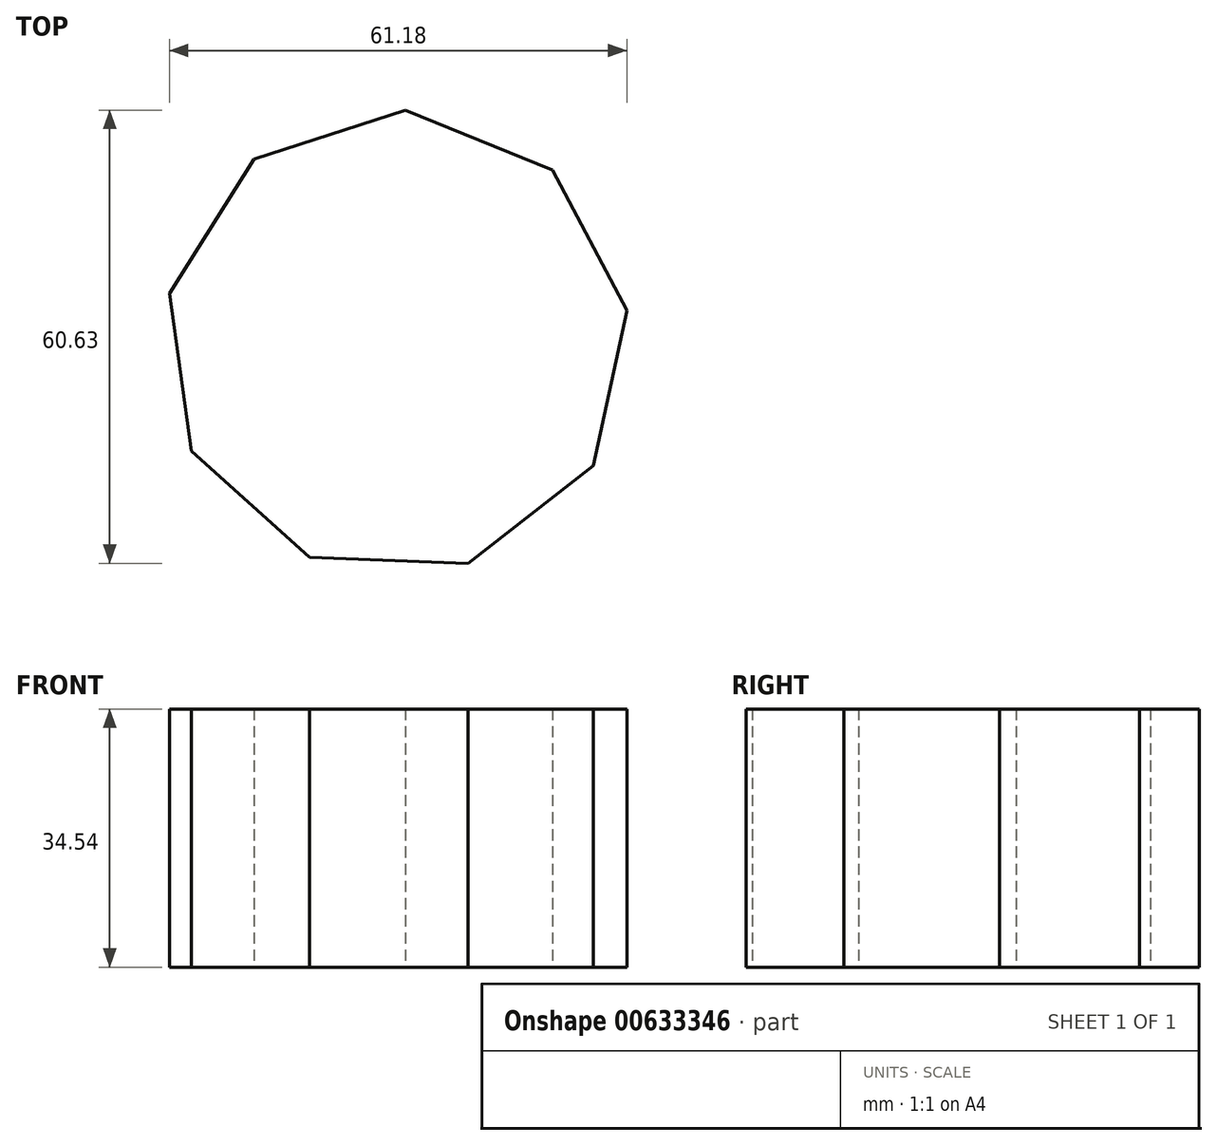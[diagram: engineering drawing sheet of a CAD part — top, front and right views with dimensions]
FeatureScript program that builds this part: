
annotation { "Feature Type Name" : "Feature", "Feature Type Description" : "" }
export const myFeature = defineFeature(function(context is Context, id is Id, definition is map)
    precondition{}
    {
        {
            var Q0;
            Q0=qCreatedBy(makeId("Top.planeOp"),FACE);
            var sketch = newSketch(context, id + "F0", { "sketchPlane" : qUnion([Q0])});
            skCircle(sketch, "E0.cCircle", {"center": v(0, -1.99) * mm, "radius": 29.2 * mm, "construction": true});
            skLineSegment(sketch, "E0.0", {"start": v(-30.39, 4.53) * mm, "end": v(-19.09, 22.54) * mm});
            skLineSegment(sketch, "E0.1", {"start": v(-19.09, 22.54) * mm, "end": v(1.14, 29.07) * mm});
            skLineSegment(sketch, "E0.2", {"start": v(1.14, 29.07) * mm, "end": v(20.84, 21.07) * mm});
            skLineSegment(sketch, "E0.3", {"start": v(20.84, 21.07) * mm, "end": v(30.79, 2.28) * mm});
            skLineSegment(sketch, "E0.4", {"start": v(30.79, 2.28) * mm, "end": v(26.33, -18.5) * mm});
            skLineSegment(sketch, "E0.5", {"start": v(26.33, -18.5) * mm, "end": v(9.55, -31.56) * mm});
            skLineSegment(sketch, "E0.6", {"start": v(9.55, -31.56) * mm, "end": v(-11.7, -30.78) * mm});
            skLineSegment(sketch, "E0.7", {"start": v(-11.7, -30.78) * mm, "end": v(-27.47, -16.53) * mm});
            skLineSegment(sketch, "E0.8", {"start": v(-27.47, -16.53) * mm, "end": v(-30.39, 4.53) * mm});
            skPoint(sketch, "E0.0.midPoint", {"position": v(-24.74, 13.53) * mm});
            skSolve(sketch);
        }
        {
            var Q0;
            Q0 = qSketchRegion(id + "F0", true);
            extrude(context, id + "F1", {"entities" : qUnion([Q0]), "depth" : 34.54 * mm, "offsetDistance" : 25.4 * mm});
        }
    });
